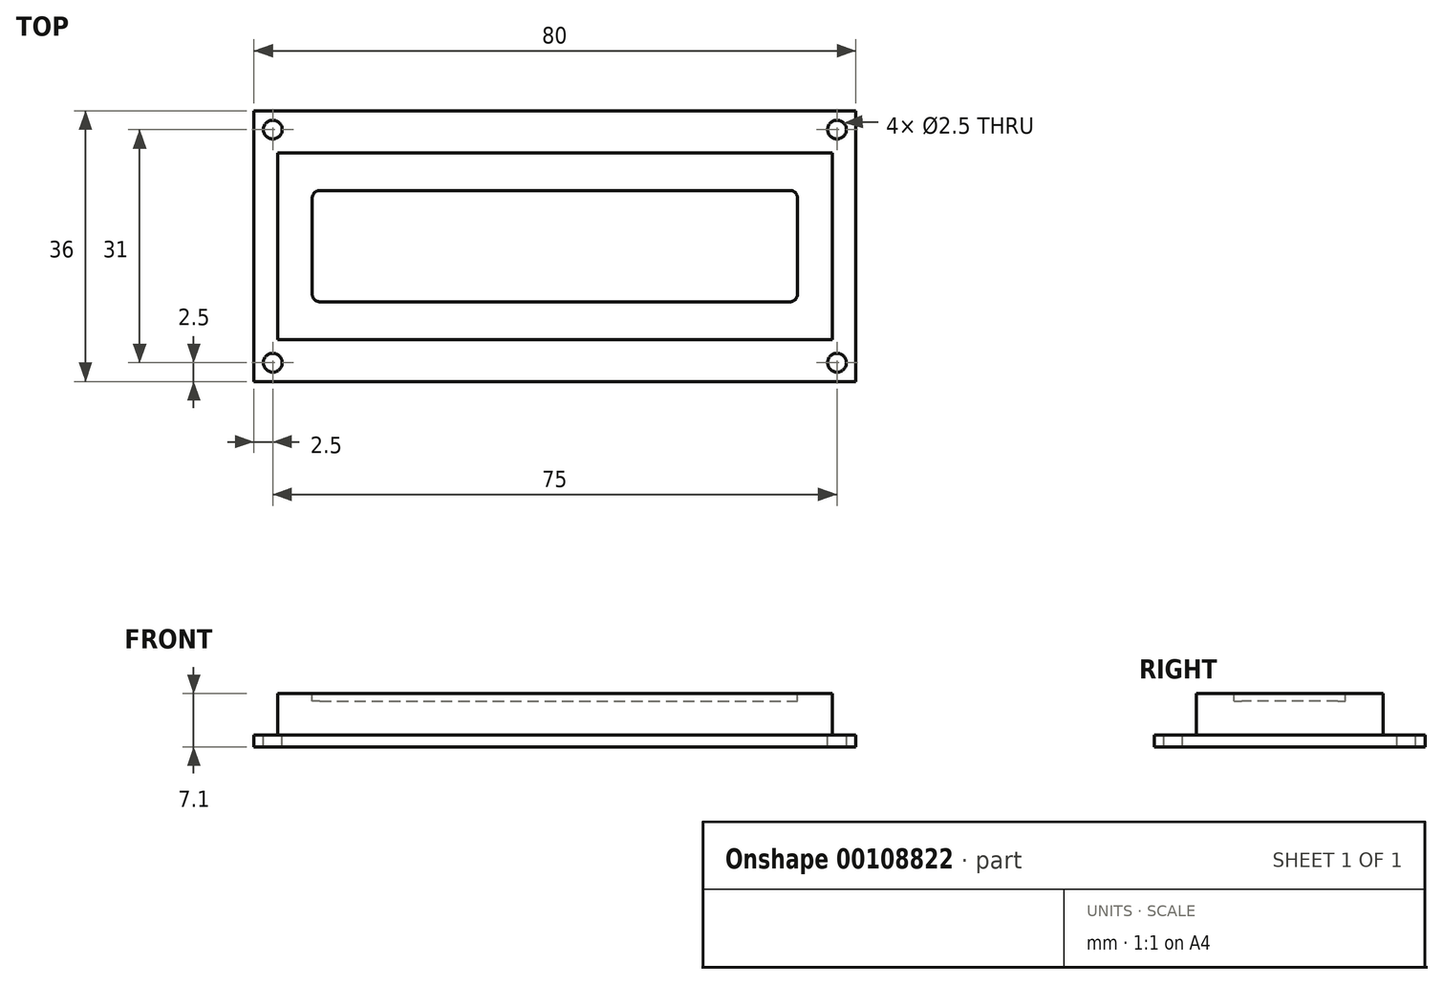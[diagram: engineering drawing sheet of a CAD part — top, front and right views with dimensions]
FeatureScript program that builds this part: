
annotation { "Feature Type Name" : "Feature", "Feature Type Description" : "" }
export const myFeature = defineFeature(function(context is Context, id is Id, definition is map)
    precondition{}
    {
        {
            var Q0;
            Q0=qCreatedBy(makeId("Top.planeOp"),FACE);
            var sketch = newSketch(context, id + "F0", { "sketchPlane" : qUnion([Q0])});
            skLineSegment(sketch, "E0.bottom", {"start": v(0, 0) * mm, "end": v(80, 0) * mm});
            skLineSegment(sketch, "E0.top", {"start": v(0, 36) * mm, "end": v(80, 36) * mm});
            skLineSegment(sketch, "E0.left", {"start": v(0, 0) * mm, "end": v(0, 36) * mm});
            skLineSegment(sketch, "E0.right", {"start": v(80, 0) * mm, "end": v(80, 36) * mm});
            skSolve(sketch);
        }
        {
            var Q0;
            Q0=makeQuery(id+"F0.imprint","IMPRINT",FACE,{"disambiguationData":[TD([[makeQuery(id+"F0.imprint","IMPRINT",EDGE,{"derivedFrom":sQuery(id+"F0.wireOp",EDGE,"E0.bottom")}),1.0]])]});
            extrude(context, id + "F1", {"entities" : qUnion([Q0]), "depth" : 1.6 * mm, "offsetDistance" : 25 * mm});
        }
        {
            var Q0;
            Q0=makeQuery(id+"F1.opExtrude","CAP_FACE",FACE,{"disambiguationData":[OSD([sQuery(id+"F0.wireOp",EDGE,"E0.bottom"),sQuery(id+"F0.wireOp",EDGE,"E0.top"),sQuery(id+"F0.wireOp",EDGE,"E0.left"),sQuery(id+"F0.wireOp",EDGE,"E0.right")])],"isStart":false});
            var sketch = newSketch(context, id + "F2", { "sketchPlane" : qUnion([Q0])});
            skCircle(sketch, "E1", {"center": v(2.5, 2.5) * mm, "radius": 1.25 * mm});
            skLineSegment(sketch, "E2", {"start": v(40, 36) * mm, "end": v(40, 0) * mm, "construction": true});
            skLineSegment(sketch, "E3", {"start": v(80, 18) * mm, "end": v(0, 18) * mm, "construction": true});
            skCircle(sketch, "E4.0.1.0", {"center": v(2.5, 33.5) * mm, "radius": 1.25 * mm});
            skCircle(sketch, "E4.1.0.0", {"center": v(77.5, 2.5) * mm, "radius": 1.25 * mm});
            skCircle(sketch, "E4.1.1.0", {"center": v(77.5, 33.5) * mm, "radius": 1.25 * mm});
            skLineSegment(sketch, "E4.direction1", {"start": v(2.5, 2.5) * mm, "end": v(77.5, 2.5) * mm, "construction": true});
            skLineSegment(sketch, "E4.direction2", {"start": v(2.5, 2.5) * mm, "end": v(2.5, 33.5) * mm, "construction": true});
            skSolve(sketch);
        }
        {
            var Q0;
            Q0 = qSketchRegion(id + "F2", true);
            extrude(context, id + "F3", {"entities" : qUnion([Q0]), "operationType" : NewBodyOperationType.REMOVE, "endBound" : BoundingType.UP_TO_NEXT, "oppositeDirection" : true, "depth" : 25 * mm, "offsetDistance" : 25 * mm});
        }
        {
            var Q0;
            Q0=makeQuery(id+"F1.opExtrude","CAP_FACE",FACE,{"disambiguationData":[OSD([sQuery(id+"F0.wireOp",EDGE,"E0.bottom"),sQuery(id+"F0.wireOp",EDGE,"E0.top"),sQuery(id+"F0.wireOp",EDGE,"E0.left"),sQuery(id+"F0.wireOp",EDGE,"E0.right")])],"isStart":false});
            var sketch = newSketch(context, id + "F4", { "sketchPlane" : qUnion([Q0])});
            skLineSegment(sketch, "E5", {"start": v(0, 18) * mm, "end": v(80, 18) * mm, "construction": true});
            skLineSegment(sketch, "E6", {"start": v(40, 36) * mm, "end": v(40, 0) * mm, "construction": true});
            skLineSegment(sketch, "E7.bottom", {"start": v(3.15, 30.4) * mm, "end": v(76.85, 30.4) * mm});
            skLineSegment(sketch, "E7.top", {"start": v(3.15, 5.6) * mm, "end": v(76.85, 5.6) * mm});
            skLineSegment(sketch, "E7.left", {"start": v(3.15, 30.4) * mm, "end": v(3.15, 5.6) * mm});
            skLineSegment(sketch, "E7.right", {"start": v(76.85, 30.4) * mm, "end": v(76.85, 5.6) * mm});
            skPoint(sketch, "E7.middle", {"position": v(40, 18) * mm});
            skSolve(sketch);
        }
        {
            var Q0;
            Q0=makeQuery(id+"F4.imprint","IMPRINT",FACE,{"disambiguationData":[TD([[makeQuery(id+"F4.imprint","IMPRINT",EDGE,{"derivedFrom":sQuery(id+"F4.wireOp",EDGE,"E7.bottom")}),-1.0]])]});
            extrude(context, id + "F5", {"entities" : qUnion([Q0]), "depth" : 5.5 * mm, "offsetDistance" : 25 * mm});
        }
        {
            var Q0;
            Q0=makeQuery(id+"F5.opExtrude","CAP_FACE",FACE,{"disambiguationData":[OSD([sQuery(id+"F4.wireOp",EDGE,"E7.bottom"),sQuery(id+"F4.wireOp",EDGE,"E7.top"),sQuery(id+"F4.wireOp",EDGE,"E7.left"),sQuery(id+"F4.wireOp",EDGE,"E7.right")])],"isStart":false});
            var sketch = newSketch(context, id + "F6", { "sketchPlane" : qUnion([Q0])});
            skLineSegment(sketch, "E8", {"start": v(3.15, 18) * mm, "end": v(76.85, 18) * mm, "construction": true});
            skLineSegment(sketch, "E9", {"start": v(40, 30.4) * mm, "end": v(40, 5.6) * mm, "construction": true});
            skLineSegment(sketch, "E10.bottom", {"start": v(7.75, 25.4) * mm, "end": v(72.25, 25.4) * mm});
            skLineSegment(sketch, "E10.top", {"start": v(7.75, 10.6) * mm, "end": v(72.25, 10.6) * mm});
            skLineSegment(sketch, "E10.left", {"start": v(7.75, 25.4) * mm, "end": v(7.75, 10.6) * mm});
            skLineSegment(sketch, "E10.right", {"start": v(72.25, 25.4) * mm, "end": v(72.25, 10.6) * mm});
            skPoint(sketch, "E10.middle", {"position": v(40, 18) * mm});
            skSolve(sketch);
        }
        {
            var Q0;
            Q0 = qSketchRegion(id + "F6", true);
            extrude(context, id + "F7", {"entities" : qUnion([Q0]), "operationType" : NewBodyOperationType.REMOVE, "oppositeDirection" : true, "depth" : 1 * mm, "offsetDistance" : 25 * mm});
        }
        {
            var Q0;
            Q0=makeQuery(id+"F7.boolean.opBoolean","COPY",EDGE,{"derivedFrom":makeQuery(id+"F7.opExtrude","SWEPT_EDGE",EDGE,{"disambiguationData":[OSD([sQuery(id+"F6.wireOp",EDGE,"E10.bottom"),sQuery(id+"F6.wireOp",EDGE,"E10.left")])]})});
            var Q1;
            Q1=makeQuery(id+"F7.boolean.opBoolean","COPY",EDGE,{"derivedFrom":makeQuery(id+"F7.opExtrude","SWEPT_EDGE",EDGE,{"disambiguationData":[OSD([sQuery(id+"F6.wireOp",EDGE,"E10.top"),sQuery(id+"F6.wireOp",EDGE,"E10.left")])]})});
            var Q2;
            Q2=makeQuery(id+"F7.boolean.opBoolean","COPY",EDGE,{"derivedFrom":makeQuery(id+"F7.opExtrude","SWEPT_EDGE",EDGE,{"disambiguationData":[OSD([sQuery(id+"F6.wireOp",EDGE,"E10.bottom"),sQuery(id+"F6.wireOp",EDGE,"E10.right")])]})});
            var Q3;
            Q3=makeQuery(id+"F7.boolean.opBoolean","COPY",EDGE,{"derivedFrom":makeQuery(id+"F7.opExtrude","SWEPT_EDGE",EDGE,{"disambiguationData":[OSD([sQuery(id+"F6.wireOp",EDGE,"E10.top"),sQuery(id+"F6.wireOp",EDGE,"E10.right")])]})});
            fillet(context, id + "F8", {"entities" : qUnion([Q0, Q1, Q2, Q3]), "tangentPropagation" : true, "radius" : 1 * mm, "defaultsChanged" : false, "vertexSettings" : [], "allowEdgeOverflow" : false});
        }
    });
